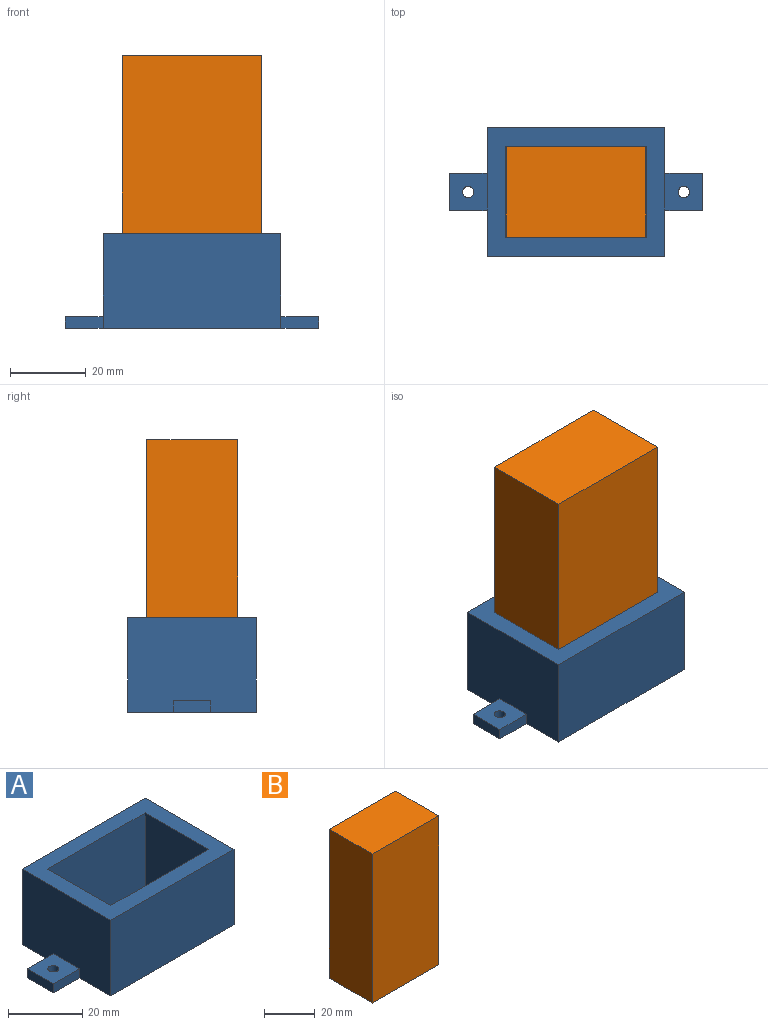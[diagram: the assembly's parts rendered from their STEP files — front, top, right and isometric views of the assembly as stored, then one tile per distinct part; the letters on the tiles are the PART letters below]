
ASSEMBLY  parts=2 mates=1
PART A: 20 faces, bbox 67x34x25 mm
  f0: plane 34x25mm, normal (1,0,0), area 820mm2, adj f4,f6,f8,f9,f10,f11,f12
  f1: plane 25x24.1mm, normal (-1,0,0), area 602.5mm2, adj f2,f7,f8,f9
  f2: plane 37.1x25mm, normal (0,1,0), area 927.5mm2, adj f1,f3,f8,f9
  f3: plane 25x24.1mm, normal (1,0,0), area 602.5mm2, adj f2,f7,f8,f9
  f4: plane 47x25mm, normal (0,1,0), area 1175mm2, adj f0,f5,f8,f9
  f5: plane 34x25mm, normal (-1,0,0), area 820mm2, adj f4,f6,f8,f9,f14,f15,f16
  f6: plane 47x25mm, normal (0,-1,0), area 1175mm2, adj f0,f5,f8,f9
  f7: plane 37.1x25mm, normal (0,-1,0), area 927.5mm2, adj f1,f3,f8,f9
  f8: plane 47x34mm, normal (0,0,1), area 703.9mm2, adj f0,f1,f2,f3,f4,f5,f6,f7
  f9: plane 67x34mm, normal (0,0,-1), area 889.8mm2, adj f0,f1,f2,f3,f4,f5,f6,f7
  f10: plane 10x10mm, normal (0,0,1), area 92.9mm2, adj f0,f11,f12,f13,f19
  f11: plane 10x3mm, normal (0,-1,0), area 30mm2, adj f0,f9,f10,f13
  f12: plane 10x3mm, normal (0,1,0), area 30mm2, adj f0,f9,f10,f13
  f13: plane 10x3mm, normal (1,0,0), area 30mm2, adj f9,f10,f11,f12
  f14: plane 10x10mm, normal (0,0,1), area 92.9mm2, adj f5,f15,f16,f17,f18
  f15: plane 10x3mm, normal (0,1,0), area 30mm2, adj f5,f9,f14,f17
  f16: plane 10x3mm, normal (0,-1,0), area 30mm2, adj f5,f9,f14,f17
  f17: plane 10x3mm, normal (-1,0,0), area 30mm2, adj f9,f14,f15,f16
  f18: cylinder r=1.5mm len=3mm, axis (0,0,1), area 28.3mm2, adj f9,f14
  f19: cylinder r=1.5mm len=3mm, axis (0,0,1), area 28.3mm2, adj f9,f10
PART B: 6 faces, bbox 37x24x72 mm
  f0: plane 72x24mm, normal (1,0,0), area 1728mm2, adj f1,f3,f4,f5
  f1: plane 72x37mm, normal (0,1,0), area 2664mm2, adj f0,f2,f4,f5
  f2: plane 72x24mm, normal (-1,0,0), area 1728mm2, adj f1,f3,f4,f5
  f3: plane 72x37mm, normal (0,-1,0), area 2664mm2, adj f0,f2,f4,f5
  f4: plane 37x24mm, normal (0,0,1), area 888mm2, adj f0,f1,f2,f3
  f5: plane 37x24mm, normal (0,0,-1), area 888mm2, adj f0,f1,f2,f3
PLACE A t=(5,5.05,0)mm
PLACE B at identity
MATE planar A.f9 <-> B.f5  axis (0,0,-1) through (-18.5,-24,0)mm
